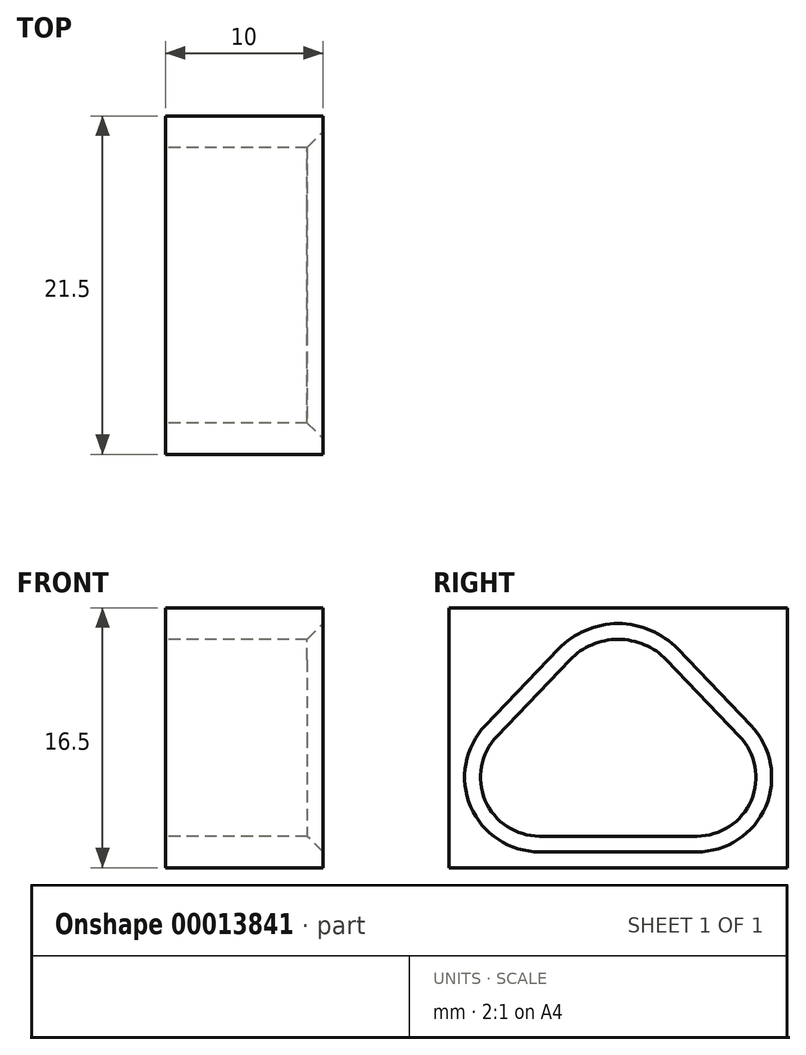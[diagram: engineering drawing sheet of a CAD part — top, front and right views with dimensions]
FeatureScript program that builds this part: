
annotation { "Feature Type Name" : "Feature", "Feature Type Description" : "" }
export const myFeature = defineFeature(function(context is Context, id is Id, definition is map)
    precondition{}
    {
        {
            var Q0;
            Q0=qCreatedBy(makeId("Right.planeOp"),FACE);
            var sketch = newSketch(context, id + "F0", { "sketchPlane" : qUnion([Q0])});
            skCircle(sketch, "E0", {"center": v(-5, 0) * mm, "radius": 3.75 * mm, "construction": true});
            skCircle(sketch, "E1", {"center": v(0, 4.5) * mm, "radius": 4.25 * mm, "construction": true});
            skCircle(sketch, "E2", {"center": v(5, 0) * mm, "radius": 3.75 * mm, "construction": true});
            skLineSegment(sketch, "E3", {"start": v(-5, -3.75) * mm, "end": v(5, -3.75) * mm});
            skLineSegment(sketch, "E4", {"start": v(-7.7, 2.6) * mm, "end": v(-3.07, 7.44) * mm});
            skArc(sketch, "E5", {"start": v(-7.7, 2.6) * mm, "mid": v(-8.45, -1.47) * mm, "end": v(-5, -3.75) * mm});
            skLineSegment(sketch, "E6.MirrorCS", {"start": v(7.7, 2.6) * mm, "end": v(3.07, 7.44) * mm});
            skArc(sketch, "E7.MirrorCS", {"start": v(7.7, 2.6) * mm, "mid": v(8.45, -1.47) * mm, "end": v(5, -3.75) * mm});
            skArc(sketch, "E8", {"start": v(-3.07, 7.44) * mm, "mid": v(0, 8.75) * mm, "end": v(3.07, 7.44) * mm});
            skLineSegment(sketch, "E9.bottom", {"start": v(-10.75, 10.75) * mm, "end": v(10.75, 10.75) * mm});
            skLineSegment(sketch, "E9.top", {"start": v(-10.75, -5.75) * mm, "end": v(10.75, -5.75) * mm});
            skLineSegment(sketch, "E9.left", {"start": v(-10.75, 10.75) * mm, "end": v(-10.75, -5.75) * mm});
            skLineSegment(sketch, "E9.right", {"start": v(10.75, 10.75) * mm, "end": v(10.75, -5.75) * mm});
            skSolve(sketch);
        }
        {
            var Q0;
            Q0 = qSketchRegion(id + "F0", true);
            extrude(context, id + "F1", {"entities" : qUnion([Q0]), "depth" : 10 * mm});
        }
        {
            var Q0;
            Q0=makeQuery(id+"F1.opExtrude","CAP_EDGE",EDGE,{"disambiguationData":[OSD([sQuery(id+"F0.wireOp",EDGE,"E3")])],"isStart":false});
            chamfer(context, id + "F2", {"entities" : qUnion([Q0]), "width" : 1 * mm, "tangentPropagation" : true});
        }
    });
